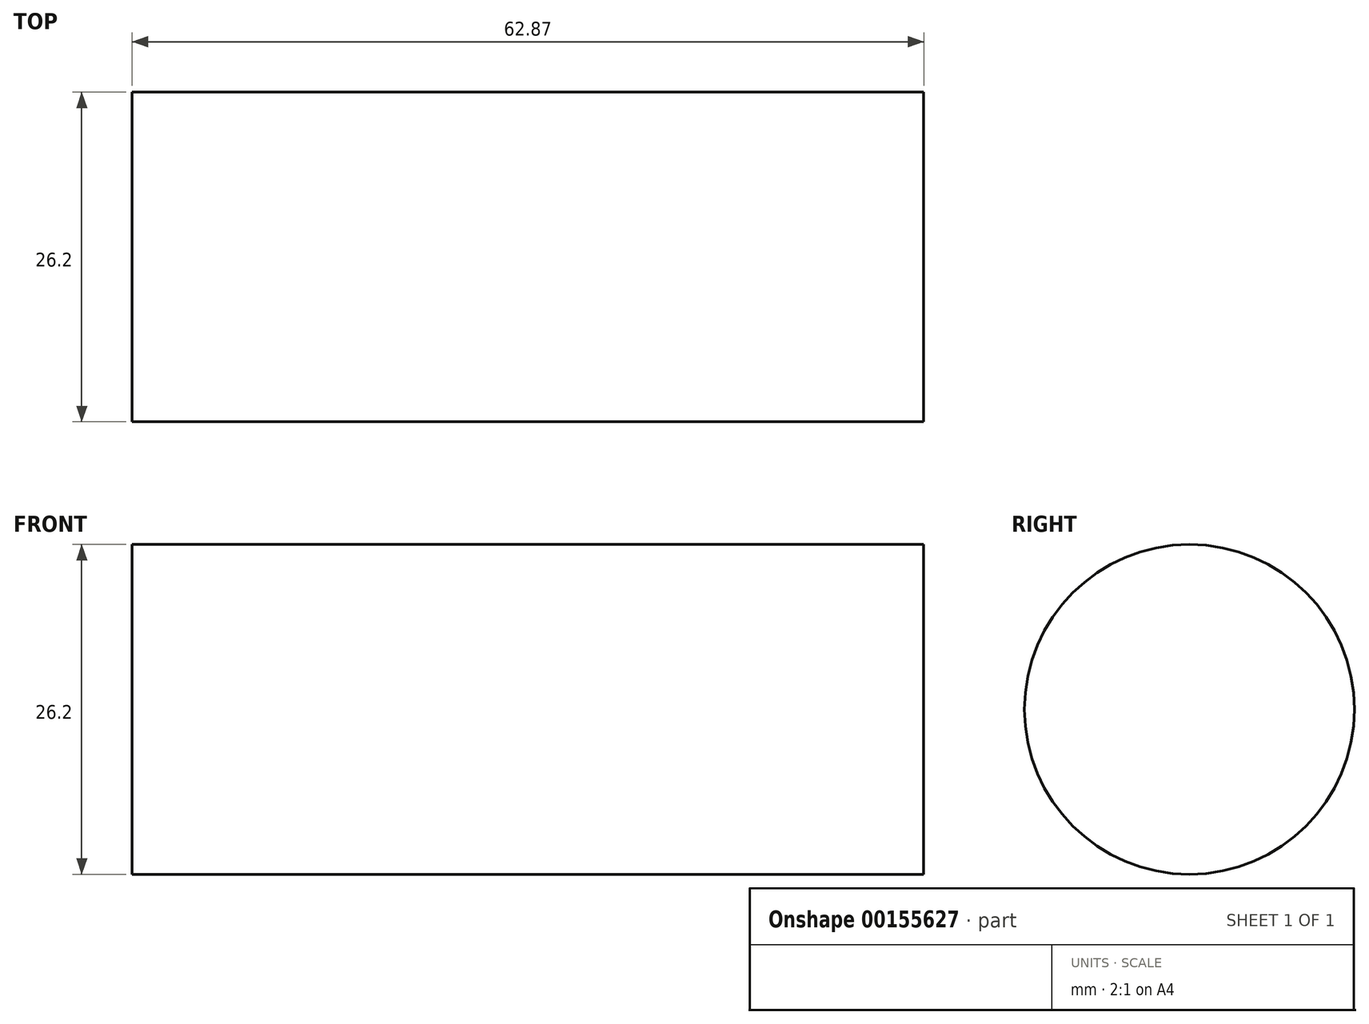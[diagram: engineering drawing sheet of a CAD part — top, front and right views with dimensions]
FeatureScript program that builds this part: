
annotation { "Feature Type Name" : "Feature", "Feature Type Description" : "" }
export const myFeature = defineFeature(function(context is Context, id is Id, definition is map)
    precondition{}
    {
        {
            var Q0;
            Q0=qCreatedBy(makeId("Right.planeOp"),FACE);
            var sketch = newSketch(context, id + "F0", { "sketchPlane" : qUnion([Q0])});
            skCircle(sketch, "E0", {"center": v(0, 0) * mm, "radius": 804.58 * mm});
            skCircle(sketch, "E1", {"center": v(0, 0) * mm, "radius": 13.1 * mm});
            skSolve(sketch);
        }
        {
            var Q0;
            Q0=makeQuery(id+"F0.imprint","IMPRINT",FACE,{"disambiguationData":[TD([[makeQuery(id+"F0.imprint","IMPRINT",EDGE,{"derivedFrom":sQuery(id+"F0.wireOp",EDGE,"E1")}),1.0]])]});
            extrude(context, id + "F1", {"entities" : qUnion([Q0]), "depth" : 62.87 * mm});
        }
    });
